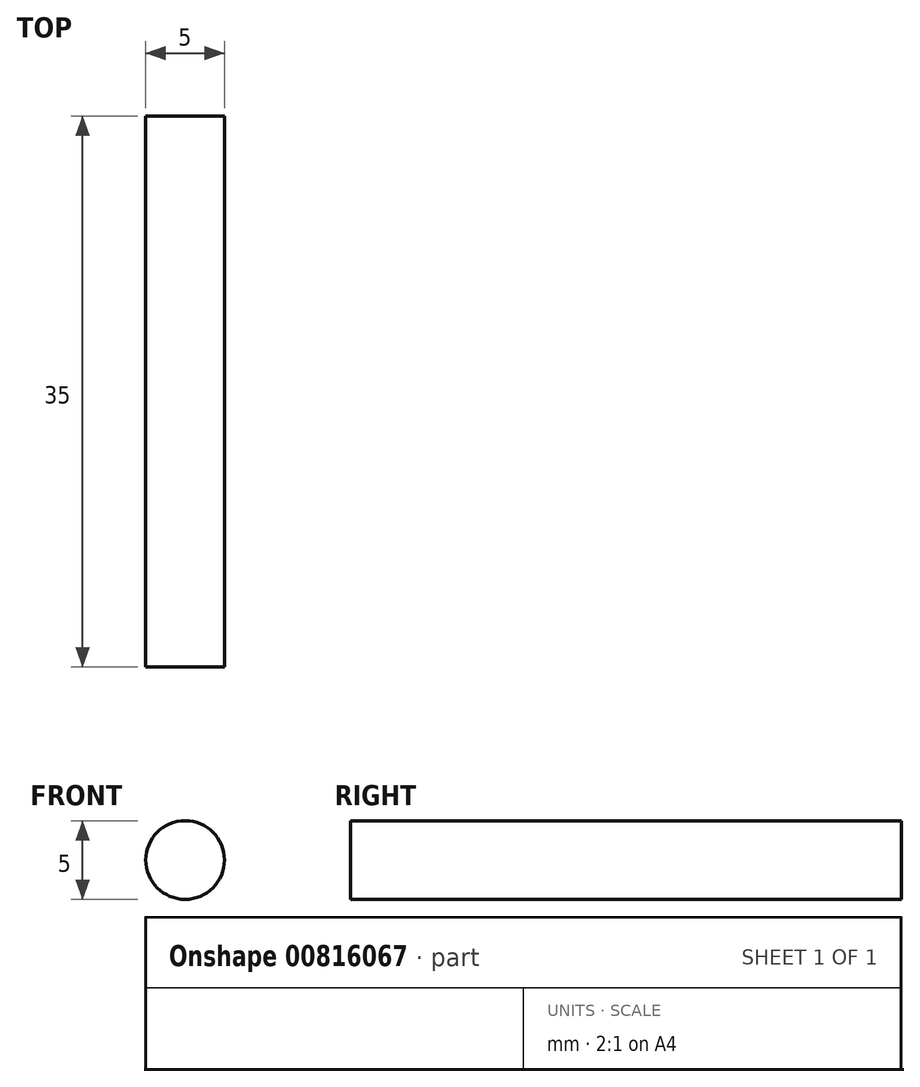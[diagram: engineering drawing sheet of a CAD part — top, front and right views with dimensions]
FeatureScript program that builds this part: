
annotation { "Feature Type Name" : "Feature", "Feature Type Description" : "" }
export const myFeature = defineFeature(function(context is Context, id is Id, definition is map)
    precondition{}
    {
        {
            var Q0;
            Q0=qCreatedBy(makeId("Front.planeOp"),FACE);
            var sketch = newSketch(context, id + "F0", { "sketchPlane" : qUnion([Q0])});
            skCircle(sketch, "E0", {"center": v(-43.85, 0) * mm, "radius": 2.5 * mm});
            skSolve(sketch);
        }
        {
            var Q0;
            Q0 = qSketchRegion(id + "F0", true);
            extrude(context, id + "F1", {"entities" : qUnion([Q0]), "depth" : 35 * mm, "offsetDistance" : 25 * mm});
        }
    });
